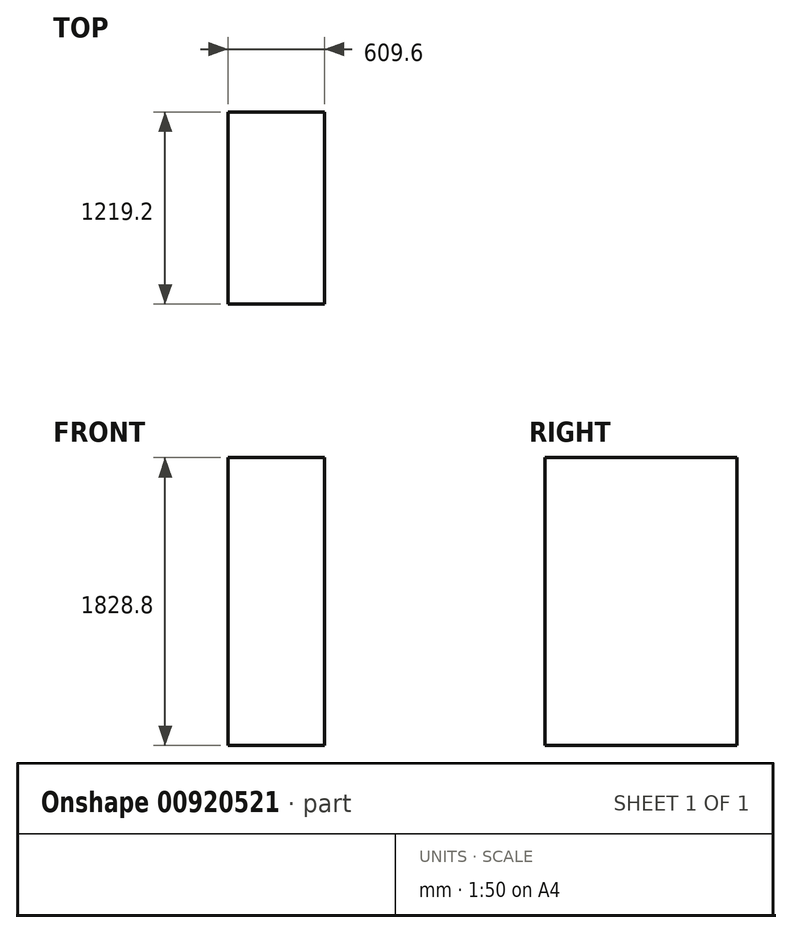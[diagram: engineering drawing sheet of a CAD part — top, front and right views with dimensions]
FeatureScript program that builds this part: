
annotation { "Feature Type Name" : "Feature", "Feature Type Description" : "" }
export const myFeature = defineFeature(function(context is Context, id is Id, definition is map)
    precondition{}
    {
        {
            var Q0;
            Q0=qCreatedBy(makeId("Top.planeOp"),FACE);
            var sketch = newSketch(context, id + "F0", { "sketchPlane" : qUnion([Q0])});
            skLineSegment(sketch, "E0.bottom", {"start": v(304.8, 609.6) * mm, "end": v(-304.8, 609.6) * mm});
            skLineSegment(sketch, "E0.top", {"start": v(304.8, -609.6) * mm, "end": v(-304.8, -609.6) * mm});
            skLineSegment(sketch, "E0.left", {"start": v(304.8, 609.6) * mm, "end": v(304.8, -609.6) * mm});
            skLineSegment(sketch, "E0.right", {"start": v(-304.8, 609.6) * mm, "end": v(-304.8, -609.6) * mm});
            skPoint(sketch, "E0.middle", {"position": v(0, 0) * mm});
            skSolve(sketch);
        }
        {
            var Q0;
            Q0 = qSketchRegion(id + "F0", true);
            extrude(context, id + "F1", {"entities" : qUnion([Q0]), "depth" : 1828.8 * mm, "offsetDistance" : 25.4 * mm});
        }
    });
